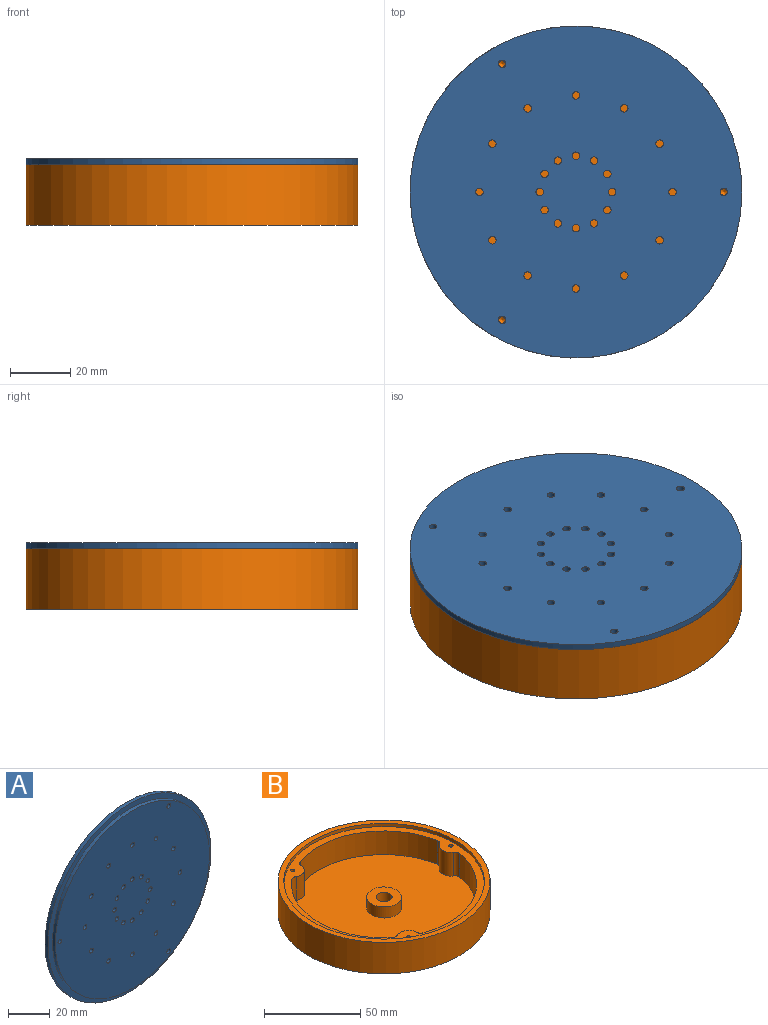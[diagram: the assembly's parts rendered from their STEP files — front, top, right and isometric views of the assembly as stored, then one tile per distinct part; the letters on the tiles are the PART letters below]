
ASSEMBLY  parts=2 mates=1
PART A: 32 faces, bbox 110x4x110 mm
  f0: cylinder r=1.25mm len=4mm, axis (0,1,0), area 31.4mm2, adj f25,f29
  f1: cylinder r=1.25mm len=4mm, axis (0,1,0), area 31.4mm2, adj f25,f29
  f2: cylinder r=1.25mm len=4mm, axis (0,1,0), area 31.4mm2, adj f25,f29
  f3: cylinder r=1.25mm len=4mm, axis (0,1,0), area 31.4mm2, adj f25,f29
  f4: cylinder r=1.25mm len=4mm, axis (0,1,0), area 31.4mm2, adj f25,f29
  f5: cylinder r=1.25mm len=4mm, axis (0,1,0), area 31.4mm2, adj f25,f29
  f6: cylinder r=1.25mm len=4mm, axis (0,1,0), area 31.4mm2, adj f25,f29
  f7: cylinder r=1.25mm len=4mm, axis (0,1,0), area 31.4mm2, adj f25,f29
  f8: cylinder r=1.25mm len=4mm, axis (0,1,0), area 31.4mm2, adj f25,f29
  f9: cylinder r=1.25mm len=4mm, axis (0,1,0), area 31.4mm2, adj f25,f29
  f10: cylinder r=1.25mm len=4mm, axis (0,1,0), area 31.4mm2, adj f25,f29
  f11: cylinder r=1.25mm len=4mm, axis (0,1,0), area 31.4mm2, adj f25,f29
  f12: cylinder r=1.25mm len=4mm, axis (0,1,0), area 31.4mm2, adj f25,f29
  f13: cylinder r=1.25mm len=4mm, axis (0,1,0), area 31.4mm2, adj f25,f29
  f14: cylinder r=1.25mm len=4mm, axis (0,1,0), area 31.4mm2, adj f25,f29
  f15: cylinder r=1.25mm len=4mm, axis (0,1,0), area 31.4mm2, adj f25,f29
  f16: cylinder r=1.25mm len=4mm, axis (0,1,0), area 31.4mm2, adj f25,f29
  f17: cylinder r=1.25mm len=4mm, axis (0,1,0), area 31.4mm2, adj f25,f29
  f18: cylinder r=1.25mm len=4mm, axis (0,1,0), area 31.4mm2, adj f25,f29
  f19: cylinder r=1.25mm len=4mm, axis (0,1,0), area 31.4mm2, adj f25,f29
  f20: cylinder r=1.25mm len=4mm, axis (0,1,0), area 31.4mm2, adj f25,f29
  f21: cylinder r=1.25mm len=4mm, axis (0,1,0), area 31.4mm2, adj f25,f29
  f22: cylinder r=1.25mm len=4mm, axis (0,1,0), area 31.4mm2, adj f25,f29
  f23: cylinder r=1.25mm len=4mm, axis (0,1,0), area 31.4mm2, adj f25,f29
  f24: cylinder r=1.25mm len=4mm, axis (0,1,0), area 31.4mm2, adj f25,f29
  f25: plane 104x104mm, normal (0,-1,0), area 8362.3mm2, adj f0,f1,f2,f3,f4,f5,f6,f7
  f26: cylinder r=52mm len=104mm, axis (0,1,0), area 653.5mm2, adj f25,f27
  f27: plane 110x110mm, normal (0,-1,0), area 1008.5mm2, adj f26,f28
  f28: cylinder r=55mm len=110mm, axis (0,1,0), area 691.2mm2, adj f27,f29
  f29: plane 110x110mm, normal (0,1,0), area 9370.8mm2, adj f0,f1,f2,f3,f4,f5,f6,f7
  f30: cylinder r=1.25mm len=4mm, axis (0,1,0), area 31.4mm2, adj f25,f29
  f31: cylinder r=1.25mm len=4mm, axis (0,1,0), area 31.4mm2, adj f25,f29
PART B: 27 faces, bbox 110x110x20 mm
  f0: plane 96x95.34mm, normal (0,0,1), area 6848.6mm2, adj f1,f2,f7,f10,f12,f13,f14,f21
  f1: cylinder r=6mm len=15mm, axis (0,0,-1), area 184.7mm2, adj f0,f9,f21,f22
  f2: cylinder r=6mm len=15mm, axis (0,0,-1), area 184.7mm2, adj f0,f9,f23,f24
  f3: cylinder r=52mm len=104mm, axis (0,0,-1), area 653.5mm2, adj f5,f9
  f4: cylinder r=55mm len=110mm, axis (0,0,-1), area 6911.5mm2, adj f5,f6
  f5: plane 110x110mm, normal (0,0,1), area 1008.5mm2, adj f3,f4
  f6: plane 110x110mm, normal (0,0,-1), area 9448.8mm2, adj f4,f11
  f7: cylinder r=9mm len=18mm, axis (0,0,-1), area 395.8mm2, adj f0,f8
  f8: plane 18x18mm, normal (0,0,1), area 199.9mm2, adj f7,f11
  f9: plane 104.11x104.01mm, normal (0,0,1), area 1380mm2, adj f1,f2,f3,f10,f12,f13,f14,f16
  f10: cylinder r=6mm len=15mm, axis (0,0,-1), area 184.7mm2, adj f0,f9,f25,f26
  f11: cylinder r=4.17mm len=10mm, axis (0,0,-1), area 261.8mm2, adj f6,f8
  f12: cylinder r=48mm len=63.83mm, axis (0,0,-1), area 1260.4mm2, adj f0,f9,f23,f26
  f13: cylinder r=48mm len=63.83mm, axis (0,0,-1), area 1260.4mm2, adj f0,f9,f22,f25
  f14: cylinder r=48mm len=73.7mm, axis (0,0,-1), area 1260.4mm2, adj f0,f9,f21,f24
  f15: cone r=0mm half-angle=59deg, axis (0,0,1), area 4.6mm2, adj f16
  f16: cylinder r=1.12mm len=10mm, axis (0,0,1), area 70.2mm2, adj f9,f15
  f17: cone r=0mm half-angle=59deg, axis (0,0,1), area 4.6mm2, adj f18
  f18: cylinder r=1.12mm len=10mm, axis (0,0,1), area 70.2mm2, adj f9,f17
  f19: cone r=0mm half-angle=59deg, axis (0,0,1), area 4.6mm2, adj f20
  f20: cylinder r=1.12mm len=10mm, axis (0,0,1), area 70.2mm2, adj f9,f19
  f21: cylinder r=3mm len=15mm, axis (0,0,-1), area 53.9mm2, adj f0,f1,f9,f14
  f22: cylinder r=3mm len=15mm, axis (0,0,1), area 53.9mm2, adj f0,f1,f9,f13
  f23: cylinder r=3mm len=15mm, axis (0,0,-1), area 53.9mm2, adj f0,f2,f9,f12
  f24: cylinder r=3mm len=15mm, axis (0,0,1), area 53.9mm2, adj f0,f2,f9,f14
  f25: cylinder r=3mm len=15mm, axis (0,0,-1), area 53.9mm2, adj f0,f9,f10,f13
  f26: cylinder r=3mm len=15mm, axis (0,0,1), area 53.9mm2, adj f0,f9,f10,f12
PLACE A rot(axis=(0.77,-0.45,-0.45),104.5deg) t=(-4.46,27.74,58)mm
PLACE B t=(-4.46,27.74,40)mm fixed
MATE revolute B.f3 <-> A.f26  axis (0,0,1) through (-4.46,27.74,60)mm
